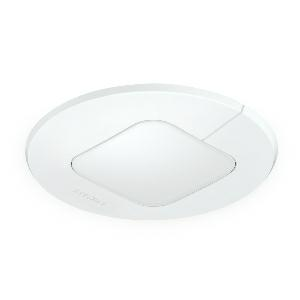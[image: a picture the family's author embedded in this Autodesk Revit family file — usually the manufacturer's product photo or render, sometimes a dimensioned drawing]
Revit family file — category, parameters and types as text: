
# Revit family: ir_quattro_slim_xs_035211
name_source: partatom
category: Elektroinstallationen
revit_build: Autodesk Revit 2016 (Build: 20190508_0715(x64)
units: mm (PartAtom-declared; Revit-internal decimal feet)

## family parameters
Basisbauteil = Fläche
Beim Laden mit Abzugskörper schneiden = Nein
Bemaßung runder Anschluss = Durchmesser verwenden
Beschriftungsausrichtung beibehalten = Nein
Gemeinsam genutzt = Nein
Raumberechnungspunkt = Nein
Teiletyp = Normal

## types (1)
- IR Quattro SLIM XS
    Apparent Load = 0 VA
    Beschreibung = Type: Presence detector; Dimensions (Ø x H): 94 x 55 mm; Mains power supply: 220 – 240 V / 50 – 60 Hz; Sensor Technology: passive infrared; Application, place: Indoors; Application, room: one-person office, hotel room, care room, function room / ancillary room, WC / washroom, Indoors; Installation site: ceiling; Installation: Concealed wiring; Switching zones: 408 switching zones; Electronic scalability: No; Mechanical scalability: No; Mounting height: 2,50 – 4,00 m; Optimum mounting height: 2,8 m; Detection angle: 360 °; Sneak-by guard: Yes; Capability of masking out individual segments: No; Reach, detail: Retina lens and hexagonal Fresnel structure; Reach, radial: 4 x 4 m (16 m²); Reach, tangential: 4 x 4 m (16 m²); Reach, presence: 4 x 4 m (16 m²); Twilight setting TEACH: Yes; Twilight setting: 10 – 1000 lx; Time setting: 30 sec – 30 min; Switching output 1, resistive: 1000 W; Switching output 1, number of LEDs / fluorescent lamps: 8 pcs.; Constant-lighting control: No; Basic light level function: No; Functions: Normal / test mode, Semi-/fully automatic, Manual ON / ON-OFF; Settings via: Remote control, Smart Remote; With remote control: Yes; Interconnection: Yes; Type of interconnection: Master/slave, Master/master; IP-rating: IP20; Material: Plastic; Ambient temperature: 0 – 40 °C; Colour: white; Colour, RAL: 9010; Manufacturer's Warranty: 5 years; Version: COM1 - round; PU1, EAN: 4007841035211
    Height = 0 mm  [stored 0 ft]
    Hersteller = Steinel
    Length = 94 mm  [stored 0.308399 ft]
    Maximum range = 2.654 m
    ModVariant = Nein
    Modell = 035211
    Mounting Place = Ceiling
    Mounting Type = Recessed
    Number of Poles = 1
    OnlyDefault = Ja
    Power Factor = 1
    Product Name = IR Quattro SLIM XS
    Product group = Presence detector
    ProductGroupID = 4
    Protection Class = Protection class
    Protection Degree = IP 20
    RlxData = <blob elided: 158309 chars, md5=fcb1dd97>
    Sensor characteristics = Circular 300°-360°
    Sensor type = Passive (infrared)
    SensorDataFile = <blob elided: 166498 chars, md5=02ce23fe>
    Type of entry = Presence, Motion
    Typenbild = produkt1_035211.jpg
    Typenkommentare = Product without accessories
    URL = http://relux.com
    VarID = ---
    Voltage = 0 V
    Vorgabe-Ansicht = 1800 mm
    Weight = 0.00 kg
    Width = 0 mm  [stored 0 ft]

note: [stored X ft] marks values corroborated as IEEE doubles in the binary element streams (Revit-internal decimal feet)

## geometry (parser evidence)
native form markers: Sweep x23
no freeform markers — native parametric forms only
